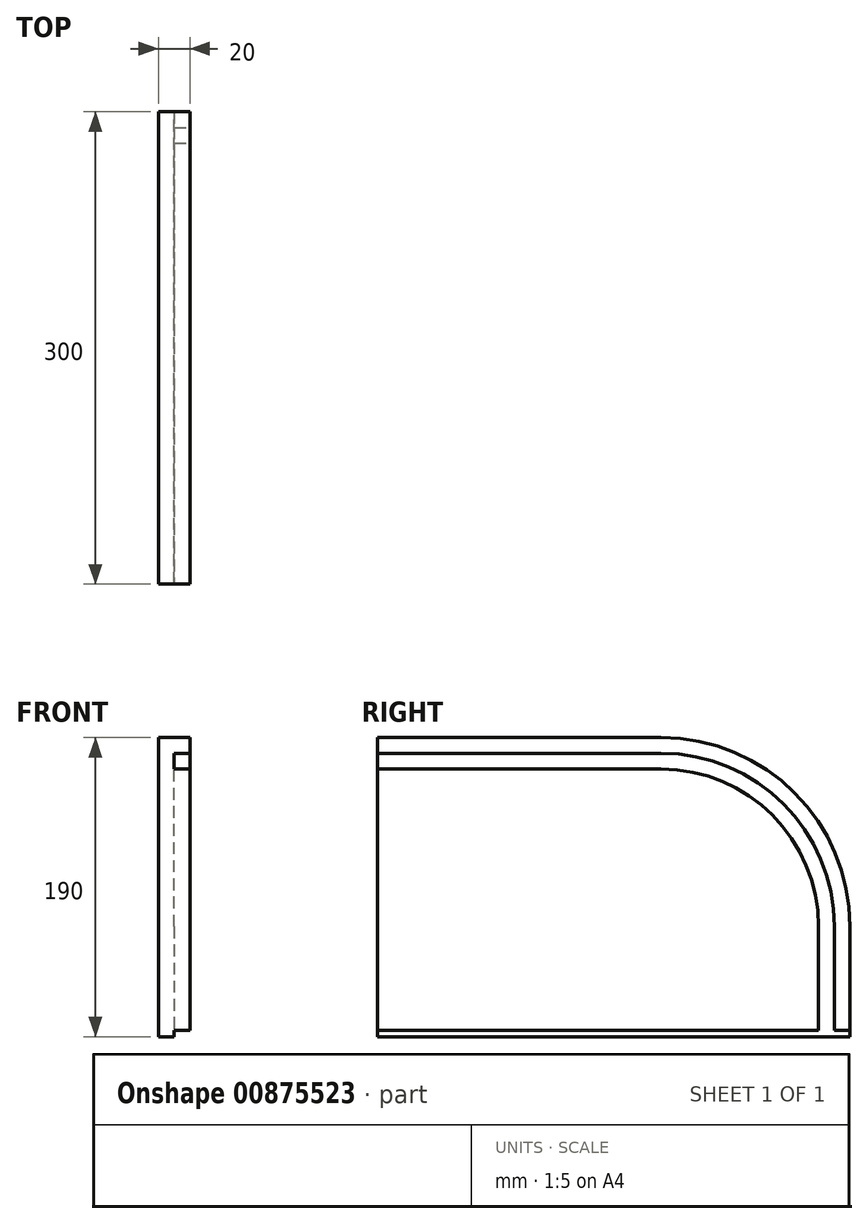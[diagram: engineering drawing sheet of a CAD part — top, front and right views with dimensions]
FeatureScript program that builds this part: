
annotation { "Feature Type Name" : "Feature", "Feature Type Description" : "" }
export const myFeature = defineFeature(function(context is Context, id is Id, definition is map)
    precondition{}
    {
        {
            var Q0;
            Q0=qCreatedBy(makeId("Right.planeOp"),FACE);
            var sketch = newSketch(context, id + "F0", { "sketchPlane" : qUnion([Q0])});
            skLineSegment(sketch, "E0.bottom", {"start": v(-149.54, 52.55) * mm, "end": v(150.46, 52.55) * mm});
            skLineSegment(sketch, "E0.top", {"start": v(-149.54, -137.45) * mm, "end": v(150.46, -137.45) * mm});
            skLineSegment(sketch, "E0.left", {"start": v(-149.54, 52.55) * mm, "end": v(-149.54, -137.45) * mm});
            skLineSegment(sketch, "E0.right", {"start": v(150.46, 52.55) * mm, "end": v(150.46, -137.45) * mm});
            skSolve(sketch);
        }
        {
            var Q0;
            Q0=makeQuery(id+"F0.imprint","IMPRINT",FACE,{"disambiguationData":[TD([[makeQuery(id+"F0.imprint","IMPRINT",EDGE,{"derivedFrom":sQuery(id+"F0.wireOp",EDGE,"E0.bottom")}),-1.0]])]});
            extrude(context, id + "F1", {"entities" : qUnion([Q0]), "depth" : 20 * mm, "offsetDistance" : 25 * mm});
        }
        {
            var Q0;
            Q0=makeQuery(id+"F1.opExtrude","SWEPT_EDGE",EDGE,{"disambiguationData":[OSD([sQuery(id+"F0.wireOp",EDGE,"E0.bottom"),sQuery(id+"F0.wireOp",EDGE,"E0.right")])]});
            fillet(context, id + "F2", {"entities" : qUnion([Q0]), "radius" : 120 * mm, "tangentPropagation" : true, "allowEdgeOverflow" : false});
        }
        {
            var Q0;
            Q0=makeQuery(id+"F1.opExtrude","CAP_FACE",FACE,{"disambiguationData":[OSD([sQuery(id+"F0.wireOp",EDGE,"E0.bottom"),sQuery(id+"F0.wireOp",EDGE,"E0.top"),sQuery(id+"F0.wireOp",EDGE,"E0.left"),sQuery(id+"F0.wireOp",EDGE,"E0.right")])],"isStart":false});
            var sketch = newSketch(context, id + "F3", { "sketchPlane" : qUnion([Q0])});
            skPoint(sketch, "E1", {"position": v(-149.54, 42.55) * mm});
            skPoint(sketch, "E2", {"position": v(30.46, 42.55) * mm});
            skLineSegment(sketch, "E3", {"start": v(-149.54, 42.55) * mm, "end": v(30.46, 42.55) * mm});
            skPoint(sketch, "E4", {"position": v(140.46, -137.45) * mm});
            skPoint(sketch, "E5", {"position": v(140.46, -67.45) * mm});
            skLineSegment(sketch, "E6", {"start": v(140.46, -67.45) * mm, "end": v(140.46, -137.45) * mm});
            skArc(sketch, "E7", {"start": v(140.46, -67.45) * mm, "mid": v(108.24, 10.33) * mm, "end": v(30.46, 42.55) * mm});
            skPoint(sketch, "E8", {"position": v(-149.54, 32.55) * mm});
            skPoint(sketch, "E9", {"position": v(30.46, 32.55) * mm});
            skPoint(sketch, "E10", {"position": v(130.46, -137.45) * mm});
            skPoint(sketch, "E11", {"position": v(130.46, -67.45) * mm});
            skLineSegment(sketch, "E12", {"start": v(-149.54, 32.55) * mm, "end": v(30.46, 32.55) * mm});
            skLineSegment(sketch, "E13", {"start": v(130.46, -67.45) * mm, "end": v(130.46, -137.45) * mm});
            skArc(sketch, "E14", {"start": v(130.46, -67.45) * mm, "mid": v(101.17, 3.26) * mm, "end": v(30.46, 32.55) * mm});
            skSolve(sketch);
        }
        {
            var Q0;
            {var subQ1=sQuery(id+"F3.wireOp",EDGE,"E3");Q0=makeQuery(id+"F3.imprint","IMPRINT",FACE,{"disambiguationData":[TD([[makeQuery(id+"F3.imprint","IMPRINT",EDGE,{"derivedFrom":subQ1}),-1.0]])]});}
            extrude(context, id + "F4", {"entities" : qUnion([Q0]), "operationType" : NewBodyOperationType.REMOVE, "oppositeDirection" : true, "depth" : 10 * mm, "offsetDistance" : 25 * mm});
        }
        {
            var Q0;
            Q0=makeQuery(id+"F1.opExtrude","SWEPT_FACE",FACE,{"disambiguationData":[OSD([sQuery(id+"F0.wireOp",EDGE,"E0.left")])]});
            var sketch = newSketch(context, id + "F5", { "sketchPlane" : qUnion([Q0])});
            skPoint(sketch, "E15", {"position": v(10, -137.45) * mm});
            skPoint(sketch, "E16", {"position": v(10, -133.45) * mm});
            skLineSegment(sketch, "E17", {"start": v(10, -137.45) * mm, "end": v(10, -133.45) * mm});
            skLineSegment(sketch, "E18", {"start": v(10, -133.45) * mm, "end": v(20, -133.45) * mm});
            skLineSegment(sketch, "E19", {"start": v(10, -133.45) * mm, "end": v(10, -137.45) * mm});
            skSolve(sketch);
        }
        {
            var Q0;
            {var subQ0=sQuery(id+"F5.wireOp",EDGE,"E18");Q0=makeQuery(id+"F5.imprint","IMPRINT",FACE,{"disambiguationData":[TD([[makeQuery(id+"F5.imprint","IMPRINT",EDGE,{"derivedFrom":subQ0}),-1.0]])]});}
            extrude(context, id + "F6", {"entities" : qUnion([Q0]), "operationType" : NewBodyOperationType.REMOVE, "oppositeDirection" : true, "depth" : 312 * mm, "offsetDistance" : 25 * mm});
        }
    });
